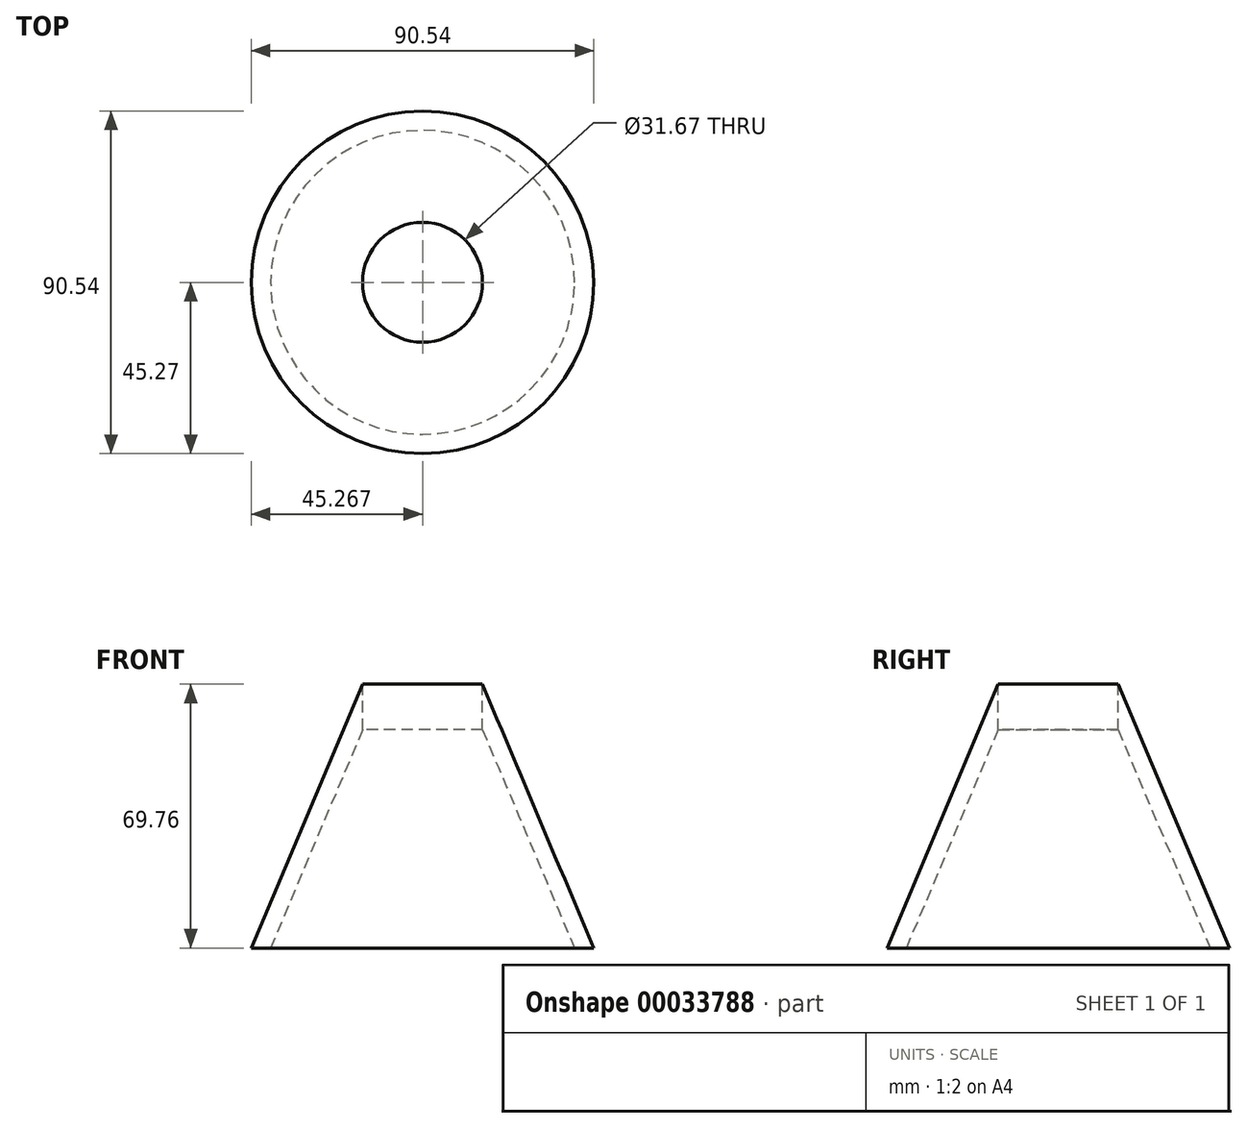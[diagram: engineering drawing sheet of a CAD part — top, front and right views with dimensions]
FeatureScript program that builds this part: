
annotation { "Feature Type Name" : "Feature", "Feature Type Description" : "" }
export const myFeature = defineFeature(function(context is Context, id is Id, definition is map)
    precondition{}
    {
        {
            var Q0;
            Q0=qCreatedBy(makeId("Front.planeOp"),FACE);
            var sketch = newSketch(context, id + "F0", { "sketchPlane" : qUnion([Q0])});
            skLineSegment(sketch, "E0", {"start": v(0, 69.76) * mm, "end": v(0, -76.1) * mm, "construction": true});
            skLineSegment(sketch, "E1", {"start": v(0, 0) * mm, "end": v(40.19, 0) * mm});
            skLineSegment(sketch, "E2", {"start": v(40.19, 0) * mm, "end": v(15.83, 57.72) * mm});
            skLineSegment(sketch, "E3", {"start": v(40.19, 0) * mm, "end": v(45.27, 0) * mm});
            skLineSegment(sketch, "E4", {"start": v(45.27, 0) * mm, "end": v(15.83, 69.76) * mm});
            skLineSegment(sketch, "E5", {"start": v(0, 69.76) * mm, "end": v(15.83, 69.76) * mm});
            skLineSegment(sketch, "E6", {"start": v(15.83, 57.72) * mm, "end": v(15.83, 69.76) * mm});
            skSolve(sketch);
        }
        {
            var Q0;
            Q0=makeQuery(id+"F0.imprint","IMPRINT",FACE,{"disambiguationData":[TD([[makeQuery(id+"F0.imprint","IMPRINT",EDGE,{"derivedFrom":sQuery(id+"F0.wireOp",EDGE,"E2")}),-1.0]])]});
            var Q1;
            Q1=sQuery(id+"F0.wireOp",EDGE,"5cf33a77-abe6-4275-852a-97a919788099");
            var Q2;
            Q2=sQuery(id+"F0.wireOp",EDGE,"61b0e3fb-f79f-4a37-8c77-a771deade353");
            var Q3;
            Q3=sQuery(id+"F0.wireOp",EDGE,"E0");
            revolve(context, id + "F1", {"entities" : qUnion([Q0]), "surfaceEntities" : qUnion([Q1, Q2]), "axis" : qUnion([Q3]), "revolveType" : RevolveType.FULL});
        }
    });
